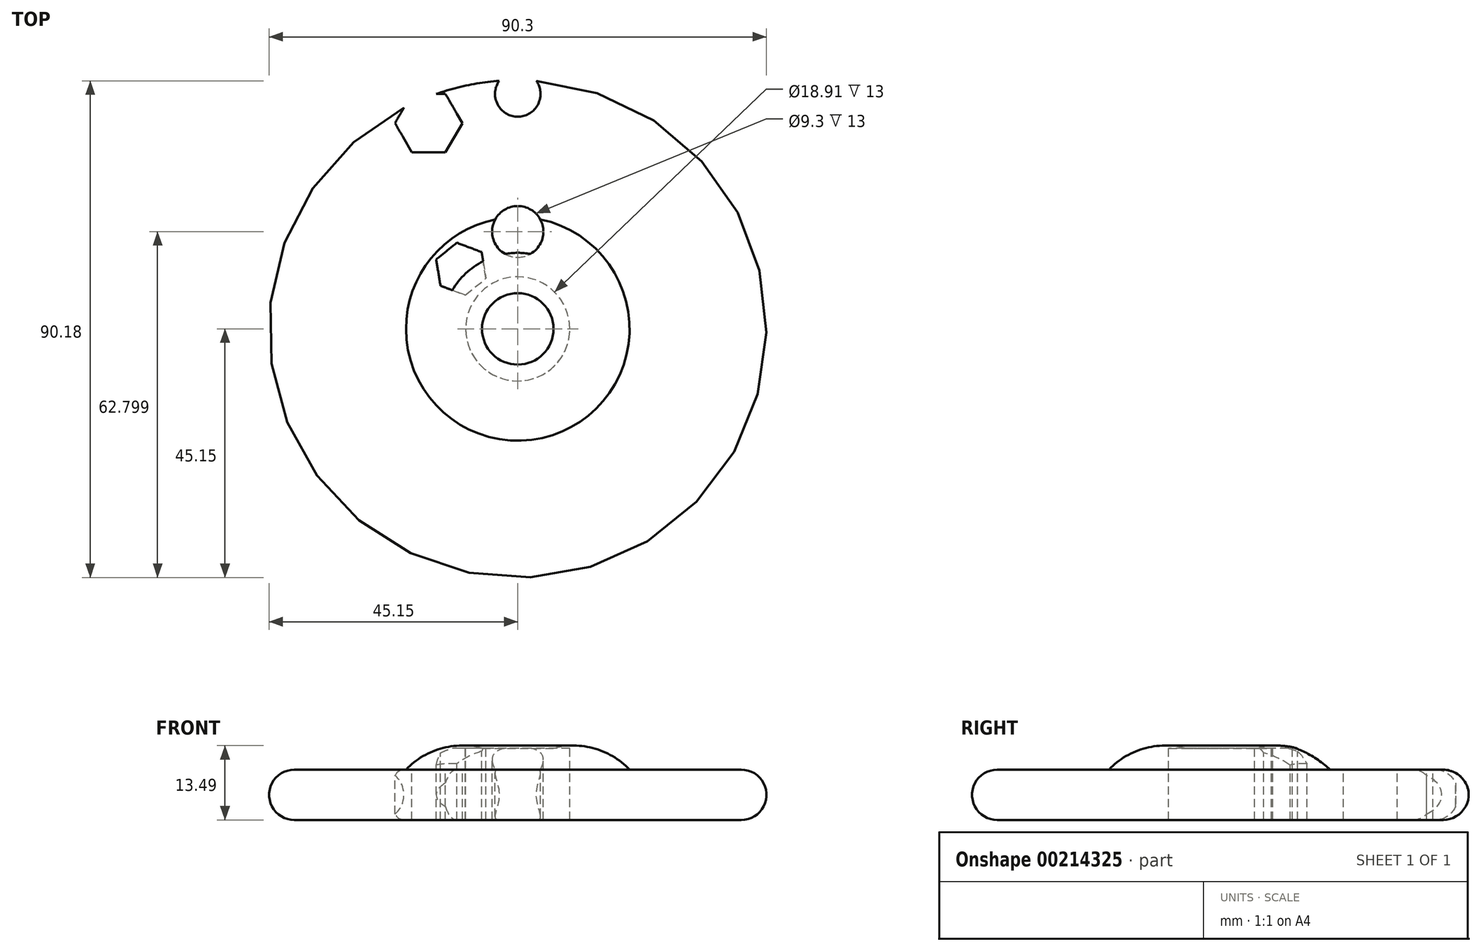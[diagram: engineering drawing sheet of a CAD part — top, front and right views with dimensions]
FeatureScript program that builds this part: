
annotation { "Feature Type Name" : "Feature", "Feature Type Description" : "" }
export const myFeature = defineFeature(function(context is Context, id is Id, definition is map)
    precondition{}
    {
        {
            var Q0;
            Q0=qCreatedBy(makeId("Front.planeOp"),FACE);
            var sketch = newSketch(context, id + "F0", { "sketchPlane" : qUnion([Q0])});
            skLineSegment(sketch, "E0.bottom", {"start": v(0, 0) * mm, "end": v(-40.6, 0) * mm});
            skLineSegment(sketch, "E0.top", {"start": v(0, 9.12) * mm, "end": v(-40.6, 9.12) * mm});
            skLineSegment(sketch, "E0.left", {"start": v(0, 0) * mm, "end": v(0, 9.12) * mm});
            skLineSegment(sketch, "E0.right", {"start": v(-40.6, 0) * mm, "end": v(-40.6, 9.12) * mm});
            skArc(sketch, "E1", {"start": v(0, 9.12) * mm, "mid": v(-10.15, 13.49) * mm, "end": v(-20.3, 9.12) * mm});
            skArc(sketch, "E2", {"start": v(-20.3, -0.48) * mm, "mid": v(-10.04, -4.61) * mm, "end": v(0, 0) * mm});
            skPoint(sketch, "E2.startSnap0", {"position": v(-20.3, 0) * mm});
            skCircle(sketch, "E3", {"center": v(-40.6, 4.56) * mm, "radius": 4.56 * mm});
            skSolve(sketch);
        }
        {
            var Q0;
            Q0 = qSketchRegion(id + "F0", true);
            var Q1;
            Q1=sQuery(id+"F0.wireOp",EDGE,"E0.left");
            revolve(context, id + "F1", {"entities" : qUnion([Q0]), "axis" : qUnion([Q1]), "revolveType" : RevolveType.FULL});
        }
        {
            var Q0;
            Q0=qCreatedBy(makeId("Top.planeOp"),FACE);
            cPlane(context, id + "F2", {"entities" : qUnion([Q0]), "cplaneType" : CPlaneType.OFFSET, "offset" : 13 * mm, "width" : 152.4 * mm, "height" : 152.4 * mm});
        }
        {
            var Q0;
            Q0=qCreatedBy(id+"F2.planeOp",FACE);
            var sketch = newSketch(context, id + "F3", { "sketchPlane" : qUnion([Q0])});
            skCircle(sketch, "E4", {"center": v(0, 42.65) * mm, "radius": 4.13 * mm});
            skSolve(sketch);
        }
        {
            var Q0;
            Q0 = qSketchRegion(id + "F3", true);
            extrude(context, id + "F4", {"entities" : qUnion([Q0]), "operationType" : NewBodyOperationType.REMOVE, "oppositeDirection" : true, "depth" : 25.4 * mm});
        }
        {
            var Q0;
            Q0=qCreatedBy(id+"F2.planeOp",FACE);
            var sketch = newSketch(context, id + "F5", { "sketchPlane" : qUnion([Q0])});
            skCircle(sketch, "E5.cCircle", {"center": v(-16.18, 37.36) * mm, "radius": 5.3 * mm, "construction": true});
            skLineSegment(sketch, "E5.0", {"start": v(-13.12, 32.06) * mm, "end": v(-19.24, 32.06) * mm});
            skLineSegment(sketch, "E5.1", {"start": v(-19.24, 32.06) * mm, "end": v(-22.3, 37.36) * mm});
            skLineSegment(sketch, "E5.2", {"start": v(-22.3, 37.36) * mm, "end": v(-19.24, 42.65) * mm});
            skLineSegment(sketch, "E5.3", {"start": v(-19.24, 42.65) * mm, "end": v(-13.12, 42.65) * mm});
            skLineSegment(sketch, "E5.4", {"start": v(-13.12, 42.65) * mm, "end": v(-10.06, 37.36) * mm});
            skLineSegment(sketch, "E5.5", {"start": v(-10.06, 37.36) * mm, "end": v(-13.12, 32.06) * mm});
            skPoint(sketch, "E5.0.midPoint", {"position": v(-16.18, 32.06) * mm});
            skSolve(sketch);
        }
        {
            var Q0;
            Q0=makeQuery(id+"F5.imprint","IMPRINT",FACE,{"disambiguationData":[TD([[makeQuery(id+"F5.imprint","IMPRINT",EDGE,{"derivedFrom":sQuery(id+"F5.wireOp",EDGE,"E5.0")}),-1.0]])]});
            extrude(context, id + "F6", {"entities" : qUnion([Q0]), "operationType" : NewBodyOperationType.REMOVE, "oppositeDirection" : true, "depth" : 25.4 * mm});
        }
        {
            var Q0;
            Q0=qCreatedBy(id+"F2.planeOp",FACE);
            var sketch = newSketch(context, id + "F7", { "sketchPlane" : qUnion([Q0])});
            skCircle(sketch, "E6", {"center": v(0, 0) * mm, "radius": 9.45 * mm});
            skSolve(sketch);
        }
        {
            var Q0;
            Q0 = qSketchRegion(id + "F7", true);
            extrude(context, id + "F8", {"entities" : qUnion([Q0]), "operationType" : NewBodyOperationType.REMOVE, "oppositeDirection" : true, "depth" : 25.4 * mm});
        }
        {
            var Q0;
            Q0=qCreatedBy(id+"F2.planeOp",FACE);
            var sketch = newSketch(context, id + "F9", { "sketchPlane" : qUnion([Q0])});
            skCircle(sketch, "E7", {"center": v(0, 17.65) * mm, "radius": 4.65 * mm});
            skSolve(sketch);
        }
        {
            var Q0;
            Q0=makeQuery(id+"F9.imprint","IMPRINT",FACE,{"disambiguationData":[TD([[makeQuery(id+"F9.imprint","IMPRINT",EDGE,{"derivedFrom":sQuery(id+"F9.wireOp",EDGE,"E7")}),1.0]])]});
            extrude(context, id + "F10", {"entities" : qUnion([Q0]), "operationType" : NewBodyOperationType.REMOVE, "oppositeDirection" : true, "depth" : 25.4 * mm});
        }
        {
            var Q0;
            Q0=qCreatedBy(id+"F2.planeOp",FACE);
            var sketch = newSketch(context, id + "F11", { "sketchPlane" : qUnion([Q0])});
            skCircle(sketch, "E8.cCircle", {"center": v(-10.3, 10.88) * mm, "radius": 4.18 * mm, "construction": true});
            skLineSegment(sketch, "E8.0", {"start": v(-5.78, 9.18) * mm, "end": v(-9.52, 6.12) * mm});
            skLineSegment(sketch, "E8.1", {"start": v(-9.52, 6.12) * mm, "end": v(-14.03, 7.83) * mm});
            skLineSegment(sketch, "E8.2", {"start": v(-14.03, 7.83) * mm, "end": v(-14.81, 12.6) * mm});
            skLineSegment(sketch, "E8.3", {"start": v(-14.81, 12.6) * mm, "end": v(-11.07, 15.65) * mm});
            skLineSegment(sketch, "E8.4", {"start": v(-11.07, 15.65) * mm, "end": v(-6.56, 13.94) * mm});
            skLineSegment(sketch, "E8.5", {"start": v(-6.56, 13.94) * mm, "end": v(-5.78, 9.18) * mm});
            skPoint(sketch, "E8.0.midPoint", {"position": v(-7.65, 7.65) * mm});
            skSolve(sketch);
        }
        {
            var Q0;
            Q0 = qSketchRegion(id + "F11", true);
            extrude(context, id + "F12", {"entities" : qUnion([Q0]), "operationType" : NewBodyOperationType.REMOVE, "oppositeDirection" : true, "depth" : 25.4 * mm});
        }
    });
